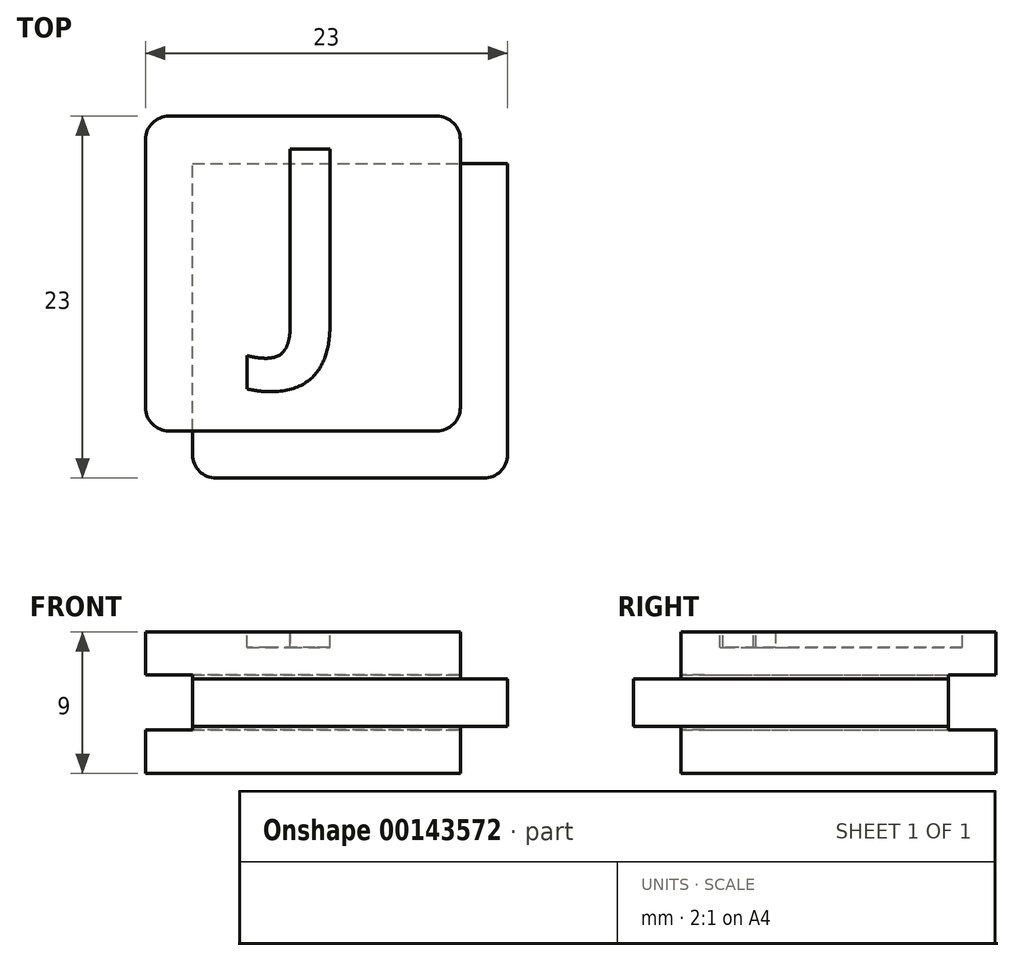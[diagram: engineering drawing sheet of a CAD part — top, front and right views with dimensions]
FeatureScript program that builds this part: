
annotation { "Feature Type Name" : "Feature", "Feature Type Description" : "" }
export const myFeature = defineFeature(function(context is Context, id is Id, definition is map)
    precondition{}
    {
        {
            var Q0;
            Q0=qCreatedBy(makeId("Front.planeOp"),FACE);
            var sketch = newSketch(context, id + "F0", { "sketchPlane" : qUnion([Q0])});
            skLineSegment(sketch, "E0.bottom", {"start": v(10, 4.5) * mm, "end": v(-10, 4.5) * mm});
            skLineSegment(sketch, "E0.top", {"start": v(10, -4.5) * mm, "end": v(-10, -4.5) * mm});
            skLineSegment(sketch, "E0.left", {"start": v(10, 4.5) * mm, "end": v(10, -4.5) * mm});
            skLineSegment(sketch, "E0.right", {"start": v(-10, 4.5) * mm, "end": v(-10, -4.5) * mm});
            skPoint(sketch, "E0.middle", {"position": v(0, 0) * mm});
            skLineSegment(sketch, "E1.bottom", {"start": v(13, 1.5) * mm, "end": v(7, 1.5) * mm});
            skLineSegment(sketch, "E1.top", {"start": v(13, -1.5) * mm, "end": v(7, -1.5) * mm});
            skLineSegment(sketch, "E1.left", {"start": v(13, 1.5) * mm, "end": v(13, -1.5) * mm});
            skLineSegment(sketch, "E1.right", {"start": v(7, 1.5) * mm, "end": v(7, -1.5) * mm});
            skPoint(sketch, "E1.middle", {"position": v(10, 0) * mm});
            skLineSegment(sketch, "E2.bottom", {"start": v(7, 1.5) * mm, "end": v(-7, 1.5) * mm});
            skLineSegment(sketch, "E2.top", {"start": v(7, -1.5) * mm, "end": v(-7, -1.5) * mm});
            skLineSegment(sketch, "E2.right", {"start": v(-7, 1.5) * mm, "end": v(-7, -1.5) * mm});
            skLineSegment(sketch, "E3.bottom", {"start": v(-7, -1.5) * mm, "end": v(-10, -1.5) * mm});
            skLineSegment(sketch, "E3.top", {"start": v(-7, 1.5) * mm, "end": v(-10, 1.5) * mm});
            skLineSegment(sketch, "E3.left", {"start": v(-7, -1.5) * mm, "end": v(-7, 1.5) * mm});
            skLineSegment(sketch, "E3.right", {"start": v(-10, -1.5) * mm, "end": v(-10, 1.5) * mm});
            skSolve(sketch);
        }
        {
            var Q0;
            {var subQ5=sQuery(id+"F0.wireOp",EDGE,"E0.bottom");Q0=makeQuery(id+"F0.imprint","IMPRINT",FACE,{"disambiguationData":[TD([[makeQuery(id+"F0.imprint","IMPRINT",EDGE,{"derivedFrom":subQ5}),1.0]])]});}
            var Q1;
            Q1=makeQuery(id+"F0.imprint","IMPRINT",FACE,{"disambiguationData":[TD([[makeQuery(id+"F0.imprint","IMPRINT",EDGE,{"derivedFrom":sQuery(id+"F0.wireOp",EDGE,"E2.bottom")}),1.0]])]});
            var Q2;
            {var subQ5=sQuery(id+"F0.wireOp",EDGE,"E1.left");Q2=makeQuery(id+"F0.imprint","IMPRINT",FACE,{"disambiguationData":[TD([[makeQuery(id+"F0.imprint","IMPRINT",EDGE,{"derivedFrom":subQ5}),-1.0]])]});}
            var Q3;
            {var subQ5=sQuery(id+"F0.wireOp",EDGE,"E1.right");Q3=makeQuery(id+"F0.imprint","IMPRINT",FACE,{"disambiguationData":[TD([[makeQuery(id+"F0.imprint","IMPRINT",EDGE,{"derivedFrom":subQ5}),1.0]])]});}
            var Q4;
            Q4=makeQuery(id+"F0.imprint","IMPRINT",FACE,{"disambiguationData":[TD([[makeQuery(id+"F0.imprint","IMPRINT",EDGE,{"derivedFrom":sQuery(id+"F0.wireOp",EDGE,"E3.bottom")}),-1.0]])]});
            var Q5;
            {var subQ5=sQuery(id+"F0.wireOp",EDGE,"E0.top");Q5=makeQuery(id+"F0.imprint","IMPRINT",FACE,{"disambiguationData":[TD([[makeQuery(id+"F0.imprint","IMPRINT",EDGE,{"derivedFrom":subQ5}),-1.0]])]});}
            extrude(context, id + "F1", {"entities" : qUnion([Q0, Q1, Q2, Q3, Q4, Q5]), "oppositeDirection" : true, "depth" : 20 * mm});
        }
        {
            var Q0;
            Q0=makeQuery(id+"F0.imprint","IMPRINT",FACE,{"disambiguationData":[TD([[makeQuery(id+"F0.imprint","IMPRINT",EDGE,{"derivedFrom":sQuery(id+"F0.wireOp",EDGE,"E3.bottom")}),-1.0]])]});
            var Q1;
            Q1=makeQuery(id+"F0.imprint","IMPRINT",FACE,{"disambiguationData":[TD([[makeQuery(id+"F0.imprint","IMPRINT",EDGE,{"derivedFrom":sQuery(id+"F0.wireOp",EDGE,"E2.bottom")}),1.0]])]});
            var Q2;
            {var subQ5=sQuery(id+"F0.wireOp",EDGE,"E1.right");Q2=makeQuery(id+"F0.imprint","IMPRINT",FACE,{"disambiguationData":[TD([[makeQuery(id+"F0.imprint","IMPRINT",EDGE,{"derivedFrom":subQ5}),1.0]])]});}
            var Q3;
            {var subQ5=sQuery(id+"F0.wireOp",EDGE,"E1.left");Q3=makeQuery(id+"F0.imprint","IMPRINT",FACE,{"disambiguationData":[TD([[makeQuery(id+"F0.imprint","IMPRINT",EDGE,{"derivedFrom":subQ5}),-1.0]])]});}
            extrude(context, id + "F2", {"entities" : qUnion([Q0, Q1, Q2, Q3]), "operationType" : NewBodyOperationType.ADD, "depth" : 3 * mm});
        }
        {
            var Q0;
            {var subQ0=sQuery(id+"F0.wireOp",EDGE,"E1.left");Q0=makeQuery(id+"F2.boolean.opBoolean","MERGE",FACE,{"derivedFrom":[makeQuery(id+"F1.opExtrude","SWEPT_FACE",FACE,{"disambiguationData":[OSD([subQ0])]}),makeQuery(id+"F2.opExtrude","SWEPT_FACE",FACE,{"disambiguationData":[OSD([subQ0])]})]});}
            var sketch = newSketch(context, id + "F3", { "sketchPlane" : qUnion([Q0])});
            skLineSegment(sketch, "E4.bottom", {"start": v(23, 1.75) * mm, "end": v(17, 1.75) * mm});
            skLineSegment(sketch, "E4.top", {"start": v(23, -1.75) * mm, "end": v(17, -1.75) * mm});
            skLineSegment(sketch, "E4.left", {"start": v(23, 1.75) * mm, "end": v(23, -1.75) * mm});
            skLineSegment(sketch, "E4.right", {"start": v(17, 1.75) * mm, "end": v(17, -1.75) * mm});
            skPoint(sketch, "E4.middle", {"position": v(20, 0) * mm});
            skSolve(sketch);
        }
        {
            var Q0;
            {var subQ1=sQuery(id+"F3.wireOp",EDGE,"E4.bottom");Q0=makeQuery(id+"F3.imprint","IMPRINT",FACE,{"disambiguationData":[TD([[makeQuery(id+"F3.imprint","IMPRINT",EDGE,{"derivedFrom":subQ1}),1.0]])]});}
            var Q1;
            {var subQ1=sQuery(id+"F0.wireOp",EDGE,"E1.left");var subQ8=makeQuery(id+"F1.opExtrude","CAP_EDGE",EDGE,{"disambiguationData":[OSD([subQ1])],"isStart":false});Q1=makeQuery(id+"F3.imprint","IMPRINT",FACE,{"disambiguationData":[TD([[makeQuery(id+"F3.imprint","IMPRINT",EDGE,{"derivedFrom":subQ8}),-1.0]])]});}
            extrude(context, id + "F4", {"entities" : qUnion([Q0, Q1]), "operationType" : NewBodyOperationType.REMOVE, "oppositeDirection" : true, "depth" : 100 * mm});
        }
        {
            var Q0;
            Q0=makeQuery(id+"F4.boolean.opBoolean","COPY",FACE,{"derivedFrom":makeQuery(id+"F4.opExtrude","SWEPT_FACE",FACE,{"disambiguationData":[OSD([sQuery(id+"F3.wireOp",EDGE,"E4.right")])]})});
            var sketch = newSketch(context, id + "F5", { "sketchPlane" : qUnion([Q0])});
            skLineSegment(sketch, "E5.bottom", {"start": v(13, 1.75) * mm, "end": v(7, 1.75) * mm});
            skLineSegment(sketch, "E5.top", {"start": v(13, -1.75) * mm, "end": v(7, -1.75) * mm});
            skLineSegment(sketch, "E5.left", {"start": v(13, 1.75) * mm, "end": v(13, -1.75) * mm});
            skLineSegment(sketch, "E5.right", {"start": v(7, 1.75) * mm, "end": v(7, -1.75) * mm});
            skPoint(sketch, "E5.middle", {"position": v(10, 0) * mm});
            skSolve(sketch);
        }
        {
            var Q0;
            {var subQ3=sQuery(id+"F5.wireOp",EDGE,"E5.left");Q0=makeQuery(id+"F5.imprint","IMPRINT",FACE,{"disambiguationData":[TD([[makeQuery(id+"F5.imprint","IMPRINT",EDGE,{"derivedFrom":subQ3}),-1.0]])]});}
            var Q1;
            {var subQ4=sQuery(id+"F5.wireOp",EDGE,"E5.right");Q1=makeQuery(id+"F5.imprint","IMPRINT",FACE,{"disambiguationData":[TD([[makeQuery(id+"F5.imprint","IMPRINT",EDGE,{"derivedFrom":subQ4}),1.0]])]});}
            extrude(context, id + "F6", {"entities" : qUnion([Q0, Q1]), "operationType" : NewBodyOperationType.REMOVE, "oppositeDirection" : true, "depth" : 100 * mm});
        }
        {
            var Q0;
            Q0=makeQuery(id+"F6.boolean.opBoolean","INTERSECT",EDGE,{"derivedFrom":[makeQuery(id+"F2.opExtrude","CAP_FACE",FACE,{"disambiguationData":[OSD([sQuery(id+"F0.wireOp",EDGE,"E1.bottom"),sQuery(id+"F0.wireOp",EDGE,"E1.top"),sQuery(id+"F0.wireOp",EDGE,"E1.left"),sQuery(id+"F0.wireOp",EDGE,"E2.bottom"),sQuery(id+"F0.wireOp",EDGE,"E2.top"),sQuery(id+"F0.wireOp",EDGE,"E3.bottom"),sQuery(id+"F0.wireOp",EDGE,"E3.top"),sQuery(id+"F0.wireOp",EDGE,"E3.right")])],"isStart":false}),makeQuery(id+"F6.opExtrude","SWEPT_FACE",FACE,{"disambiguationData":[OSD([sQuery(id+"F5.wireOp",EDGE,"E5.right")])]})]});
            var Q1;
            Q1=makeQuery(id+"F2.opExtrude","CAP_EDGE",EDGE,{"disambiguationData":[OSD([sQuery(id+"F0.wireOp",EDGE,"E1.left")])],"isStart":false});
            var Q2;
            {var subQ0=sQuery(id+"F0.wireOp",EDGE,"E0.left");Q2=makeQuery(id+"F1.opExtrude","CAP_EDGE",EDGE,{"disambiguationData":[OSD([subQ0]),TDD([makeQuery(id+"F0.imprint","IMPRINT",EDGE,{"disambiguationData":[TD([[makeQuery(id+"F0.imprint","INTERSECT",VERTEX,{"derivedFrom":[sQuery(id+"F0.wireOp",EDGE,"E0.bottom"),subQ0]}),-1.0]])],"derivedFrom":subQ0})])],"isStart":true});}
            var Q3;
            {var subQ0=sQuery(id+"F0.wireOp",EDGE,"E0.left");Q3=makeQuery(id+"F1.opExtrude","CAP_EDGE",EDGE,{"disambiguationData":[OSD([subQ0]),TDD([makeQuery(id+"F0.imprint","IMPRINT",EDGE,{"disambiguationData":[TD([[makeQuery(id+"F0.imprint","INTERSECT",VERTEX,{"derivedFrom":[sQuery(id+"F0.wireOp",EDGE,"E0.top"),subQ0]}),1.0]])],"derivedFrom":subQ0})])],"isStart":true});}
            var Q4;
            {var subQ0=sQuery(id+"F0.wireOp",EDGE,"E3.right");var subQ1=sQuery(id+"F0.wireOp",EDGE,"E0.right");var subQ3=sQuery(id+"F0.wireOp",EDGE,"E0.top");Q4=makeQuery(id+"F2.boolean.opBoolean","SPLIT",EDGE,{"disambiguationData":[TD([makeQuery(id+"F1.opExtrude","SWEPT_FACE",FACE,{"disambiguationData":[OSD([subQ3])]})])],"derivedFrom":makeQuery(id+"F1.opExtrude","CAP_EDGE",EDGE,{"disambiguationData":[OSD([subQ1,subQ0])],"isStart":true})});}
            var Q5;
            {var subQ1=sQuery(id+"F0.wireOp",EDGE,"E3.right");var subQ2=sQuery(id+"F0.wireOp",EDGE,"E0.right");var subQ3=sQuery(id+"F0.wireOp",EDGE,"E0.bottom");Q5=makeQuery(id+"F2.boolean.opBoolean","SPLIT",EDGE,{"disambiguationData":[TD([makeQuery(id+"F1.opExtrude","SWEPT_FACE",FACE,{"disambiguationData":[OSD([subQ3])]})])],"derivedFrom":makeQuery(id+"F1.opExtrude","CAP_EDGE",EDGE,{"disambiguationData":[OSD([subQ2,subQ1])],"isStart":true})});}
            var Q6;
            Q6=makeQuery(id+"F6.boolean.opBoolean","COPY",EDGE,{"derivedFrom":makeQuery(id+"F6.opExtrude","CAP_EDGE",EDGE,{"disambiguationData":[OSD([sQuery(id+"F5.wireOp",EDGE,"E5.right")])],"isStart":true})});
            var Q7;
            {var subQ0=sQuery(id+"F0.wireOp",EDGE,"E3.right");var subQ1=sQuery(id+"F0.wireOp",EDGE,"E0.right");var subQ2=sQuery(id+"F0.wireOp",EDGE,"E0.bottom");Q7=makeQuery(id+"F4.boolean.opBoolean","SPLIT",EDGE,{"disambiguationData":[TD([makeQuery(id+"F1.opExtrude","SWEPT_FACE",FACE,{"disambiguationData":[OSD([subQ2])]})])],"derivedFrom":makeQuery(id+"F1.opExtrude","CAP_EDGE",EDGE,{"disambiguationData":[OSD([subQ1,subQ0])],"isStart":false})});}
            var Q8;
            {var subQ0=sQuery(id+"F0.wireOp",EDGE,"E3.right");var subQ1=sQuery(id+"F0.wireOp",EDGE,"E0.right");var subQ2=sQuery(id+"F0.wireOp",EDGE,"E0.top");Q8=makeQuery(id+"F4.boolean.opBoolean","SPLIT",EDGE,{"disambiguationData":[TD([makeQuery(id+"F1.opExtrude","SWEPT_FACE",FACE,{"disambiguationData":[OSD([subQ2])]})])],"derivedFrom":makeQuery(id+"F1.opExtrude","CAP_EDGE",EDGE,{"disambiguationData":[OSD([subQ1,subQ0])],"isStart":false})});}
            var Q9;
            Q9=makeQuery(id+"F4.boolean.opBoolean","COPY",EDGE,{"derivedFrom":makeQuery(id+"F4.opExtrude","CAP_EDGE",EDGE,{"disambiguationData":[OSD([sQuery(id+"F3.wireOp",EDGE,"E4.right")])],"isStart":true})});
            var Q10;
            {var subQ0=sQuery(id+"F0.wireOp",EDGE,"E0.left");Q10=makeQuery(id+"F1.opExtrude","CAP_EDGE",EDGE,{"disambiguationData":[OSD([subQ0]),TDD([makeQuery(id+"F0.imprint","IMPRINT",EDGE,{"disambiguationData":[TD([[makeQuery(id+"F0.imprint","INTERSECT",VERTEX,{"derivedFrom":[sQuery(id+"F0.wireOp",EDGE,"E0.bottom"),subQ0]}),-1.0]])],"derivedFrom":subQ0})])],"isStart":false});}
            var Q11;
            {var subQ0=sQuery(id+"F0.wireOp",EDGE,"E0.left");Q11=makeQuery(id+"F1.opExtrude","CAP_EDGE",EDGE,{"disambiguationData":[OSD([subQ0]),TDD([makeQuery(id+"F0.imprint","IMPRINT",EDGE,{"disambiguationData":[TD([[makeQuery(id+"F0.imprint","INTERSECT",VERTEX,{"derivedFrom":[sQuery(id+"F0.wireOp",EDGE,"E0.top"),subQ0]}),1.0]])],"derivedFrom":subQ0})])],"isStart":false});}
            fillet(context, id + "F7", {"entities" : qUnion([Q0, Q1, Q2, Q3, Q4, Q5, Q6, Q7, Q8, Q9, Q10, Q11]), "radius" : 1.5 * mm, "tangentPropagation" : true, "allowEdgeOverflow" : false});
        }
        {
            var Q0;
            Q0=makeQuery(id+"F1.opExtrude","SWEPT_FACE",FACE,{"disambiguationData":[OSD([sQuery(id+"F0.wireOp",EDGE,"E0.bottom")])]});
            var sketch = newSketch(context, id + "F8", { "sketchPlane" : qUnion([Q0])});
            skText(sketch, "E6", { "text": "J", "fontName": "OpenSans-Bold.ttf"});
            skLineSegment(sketch, "E7.0", {"start": v(12.8, 6) * mm, "end": v(-11.07, 6) * mm});
            const initialGuessF8  = {"E6": [-0.0023, 0.006, 1, 0, 0.012]};
            skSetInitialGuess(sketch, initialGuessF8);
            skSolve(sketch);
        }
        {
            var Q0;
            Q0=makeQuery(id+"F8.imprint","IMPRINT",FACE,{"disambiguationData":[TD([[makeQuery(id+"F8.imprint","IMPRINT",EDGE,{"derivedFrom":sQuery(id+"F8.wireOp",EDGE,"E6.sketch_text.stroke-0")}),-1.0]])]});
            extrude(context, id + "F9", {"entities" : qUnion([Q0]), "operationType" : NewBodyOperationType.REMOVE, "oppositeDirection" : true, "depth" : 1 * mm});
        }
        {
            var Q0;
            {var subQ1=sQuery(id+"F8.wireOp",EDGE,"E6.sketch_text.stroke-5");Q0=makeQuery(id+"F8.imprint","IMPRINT",FACE,{"disambiguationData":[TD([[makeQuery(id+"F8.imprint","IMPRINT",EDGE,{"derivedFrom":subQ1}),-1.0]])]});}
            extrude(context, id + "F10", {"entities" : qUnion([Q0]), "operationType" : NewBodyOperationType.REMOVE, "oppositeDirection" : true, "depth" : 1 * mm});
        }
    });
